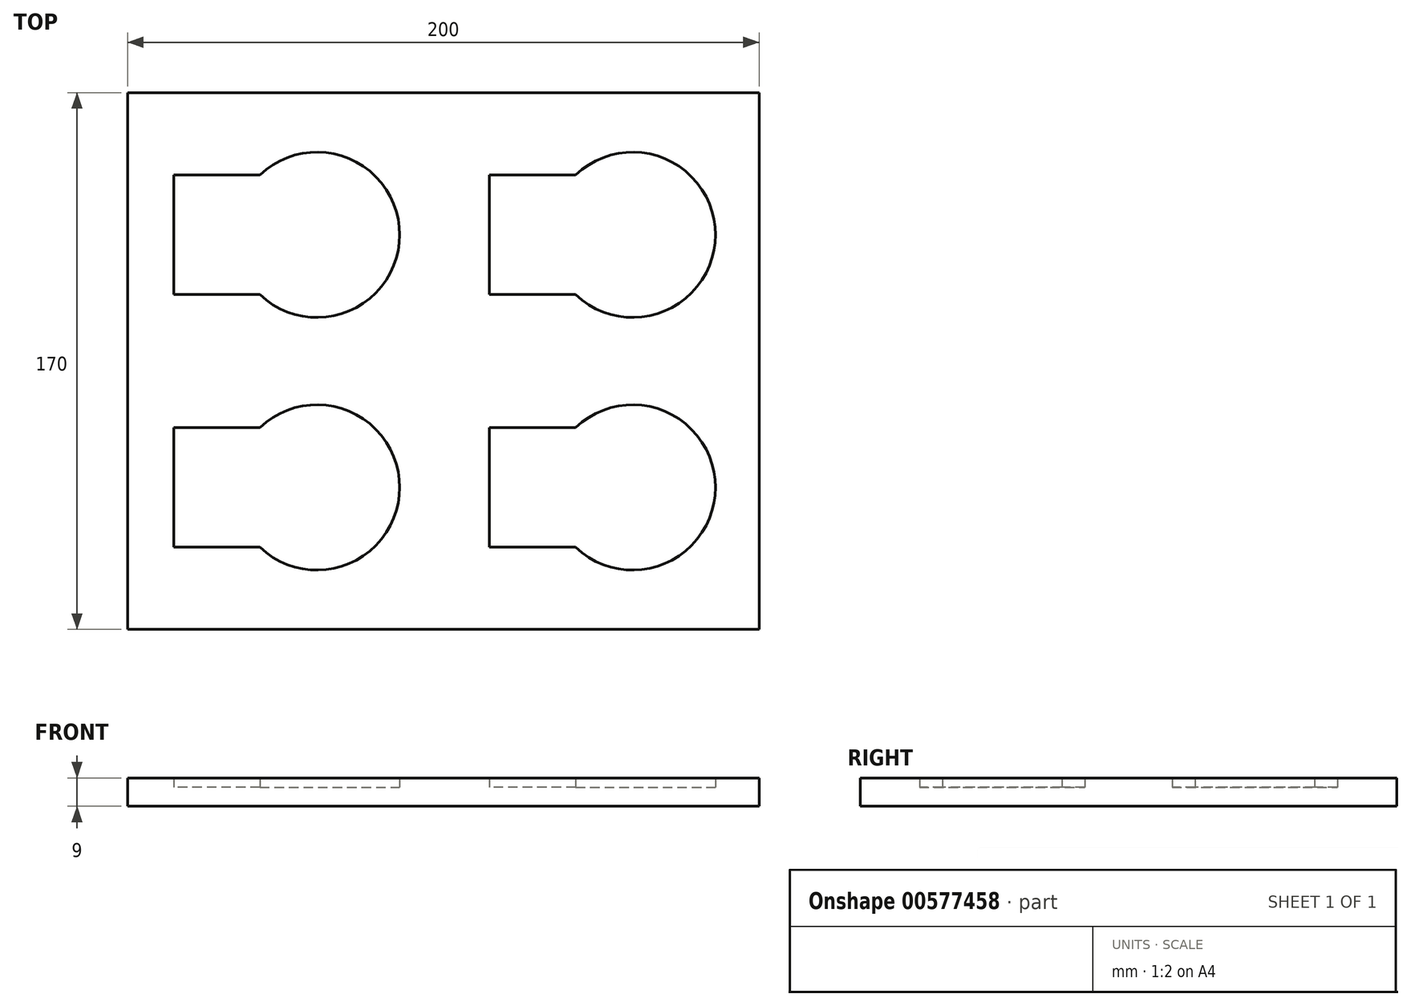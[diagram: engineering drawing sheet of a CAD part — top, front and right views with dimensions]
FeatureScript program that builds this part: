
annotation { "Feature Type Name" : "Feature", "Feature Type Description" : "" }
export const myFeature = defineFeature(function(context is Context, id is Id, definition is map)
    precondition{}
    {
        {
            var Q0;
            Q0=qCreatedBy(makeId("Top.planeOp"),FACE);
            var sketch = newSketch(context, id + "F0", { "sketchPlane" : qUnion([Q0])});
            skLineSegment(sketch, "E0.bottom", {"start": v(-100, 85) * mm, "end": v(100, 85) * mm});
            skLineSegment(sketch, "E0.top", {"start": v(-100, -85) * mm, "end": v(100, -85) * mm});
            skLineSegment(sketch, "E0.left", {"start": v(-100, 85) * mm, "end": v(-100, -85) * mm});
            skLineSegment(sketch, "E0.right", {"start": v(100, 85) * mm, "end": v(100, -85) * mm});
            skLineSegment(sketch, "E1", {"start": v(0, 0) * mm, "end": v(100, 0) * mm});
            skLineSegment(sketch, "E2", {"start": v(0, 0) * mm, "end": v(0, 85) * mm});
            skSolve(sketch);
        }
        {
            var Q0;
            {var subQ1=sQuery(id+"F0.wireOp",EDGE,"E0.top");Q0=makeQuery(id+"F0.imprint","IMPRINT",FACE,{"disambiguationData":[TD([[makeQuery(id+"F0.imprint","IMPRINT",EDGE,{"derivedFrom":subQ1}),1.0]])]});}
            var Q1;
            {var subQ4=sQuery(id+"F0.wireOp",EDGE,"E1");Q1=makeQuery(id+"F0.imprint","IMPRINT",FACE,{"disambiguationData":[TD([[makeQuery(id+"F0.imprint","IMPRINT",EDGE,{"derivedFrom":subQ4}),1.0]])]});}
            extrude(context, id + "F1", {"entities" : qUnion([Q0, Q1]), "depth" : 6 * mm, "offsetDistance" : 25.4 * mm});
        }
        {
            var Q0;
            Q0=makeQuery(id+"F1.opExtrude","CAP_FACE",FACE,{"disambiguationData":[OSD([sQuery(id+"F0.wireOp",EDGE,"E0.bottom"),sQuery(id+"F0.wireOp",EDGE,"E0.top"),sQuery(id+"F0.wireOp",EDGE,"E0.left"),sQuery(id+"F0.wireOp",EDGE,"E0.right")])],"isStart":false});
            var sketch = newSketch(context, id + "F2", { "sketchPlane" : qUnion([Q0])});
            skArc(sketch, "E3", {"start": v(-55.94, 26.06) * mm, "mid": v(-18.83, 40) * mm, "end": v(-55.94, 53.94) * mm});
            skLineSegment(sketch, "E4.bottom", {"start": v(-55.94, 53.94) * mm, "end": v(-80.38, 53.94) * mm});
            skLineSegment(sketch, "E4.top", {"start": v(-55.94, 26.06) * mm, "end": v(-80.37, 26.06) * mm});
            skLineSegment(sketch, "E4.right", {"start": v(-80.38, 53.94) * mm, "end": v(-80.38, 26.06) * mm});
            skPoint(sketch, "E5.orphan", {"position": v(-40, 53.94) * mm});
            skPoint(sketch, "E6.orphan", {"position": v(-40, 26.06) * mm});
            skArc(sketch, "E7.0", {"start": v(-58.07, 21.06) * mm, "mid": v(-13.83, 40) * mm, "end": v(-58.07, 58.94) * mm});
            skLineSegment(sketch, "E7.1", {"start": v(-58.07, 21.06) * mm, "end": v(-85.38, 21.06) * mm});
            skLineSegment(sketch, "E7.2", {"start": v(-85.38, 58.94) * mm, "end": v(-85.38, 21.06) * mm});
            skLineSegment(sketch, "E7.3", {"start": v(-58.07, 58.94) * mm, "end": v(-85.38, 58.94) * mm});
            skArc(sketch, "E8.0.1.0", {"start": v(-58.07, -58.94) * mm, "mid": v(-13.83, -40) * mm, "end": v(-58.07, -21.06) * mm});
            skLineSegment(sketch, "E8.0.1.1", {"start": v(-58.07, -21.06) * mm, "end": v(-85.38, -21.06) * mm});
            skLineSegment(sketch, "E8.0.1.2", {"start": v(-85.38, -21.06) * mm, "end": v(-85.38, -58.94) * mm});
            skLineSegment(sketch, "E8.0.1.3", {"start": v(-58.07, -58.94) * mm, "end": v(-85.38, -58.94) * mm});
            skArc(sketch, "E8.1.0.0", {"start": v(41.93, 21.06) * mm, "mid": v(86.17, 40) * mm, "end": v(41.93, 58.94) * mm});
            skLineSegment(sketch, "E8.1.0.1", {"start": v(41.93, 58.94) * mm, "end": v(14.62, 58.94) * mm});
            skLineSegment(sketch, "E8.1.0.2", {"start": v(14.62, 58.94) * mm, "end": v(14.62, 21.06) * mm});
            skLineSegment(sketch, "E8.1.0.3", {"start": v(41.93, 21.06) * mm, "end": v(14.62, 21.06) * mm});
            skArc(sketch, "E8.1.1.0", {"start": v(41.93, -58.94) * mm, "mid": v(86.17, -40) * mm, "end": v(41.93, -21.06) * mm});
            skLineSegment(sketch, "E8.1.1.1", {"start": v(41.93, -21.06) * mm, "end": v(14.62, -21.06) * mm});
            skLineSegment(sketch, "E8.1.1.2", {"start": v(14.62, -21.06) * mm, "end": v(14.62, -58.94) * mm});
            skLineSegment(sketch, "E8.1.1.3", {"start": v(41.93, -58.94) * mm, "end": v(14.62, -58.94) * mm});
            skLineSegment(sketch, "E8.direction1", {"start": v(-58.07, 21.06) * mm, "end": v(41.93, 21.06) * mm, "construction": true});
            skLineSegment(sketch, "E8.direction2", {"start": v(-58.07, 21.06) * mm, "end": v(-58.07, -58.94) * mm, "construction": true});
            skSolve(sketch);
        }
        {
            var Q0;
            Q0=makeQuery(id+"F2.imprint","IMPRINT",FACE,{"disambiguationData":[TD([[makeQuery(id+"F2.imprint","IMPRINT",EDGE,{"derivedFrom":sQuery(id+"F2.wireOp",EDGE,"E7.0")}),-1.0]])]});
            extrude(context, id + "F3", {"entities" : qUnion([Q0]), "operationType" : NewBodyOperationType.ADD, "depth" : 3 * mm, "offsetDistance" : 25 * mm});
        }
    });
